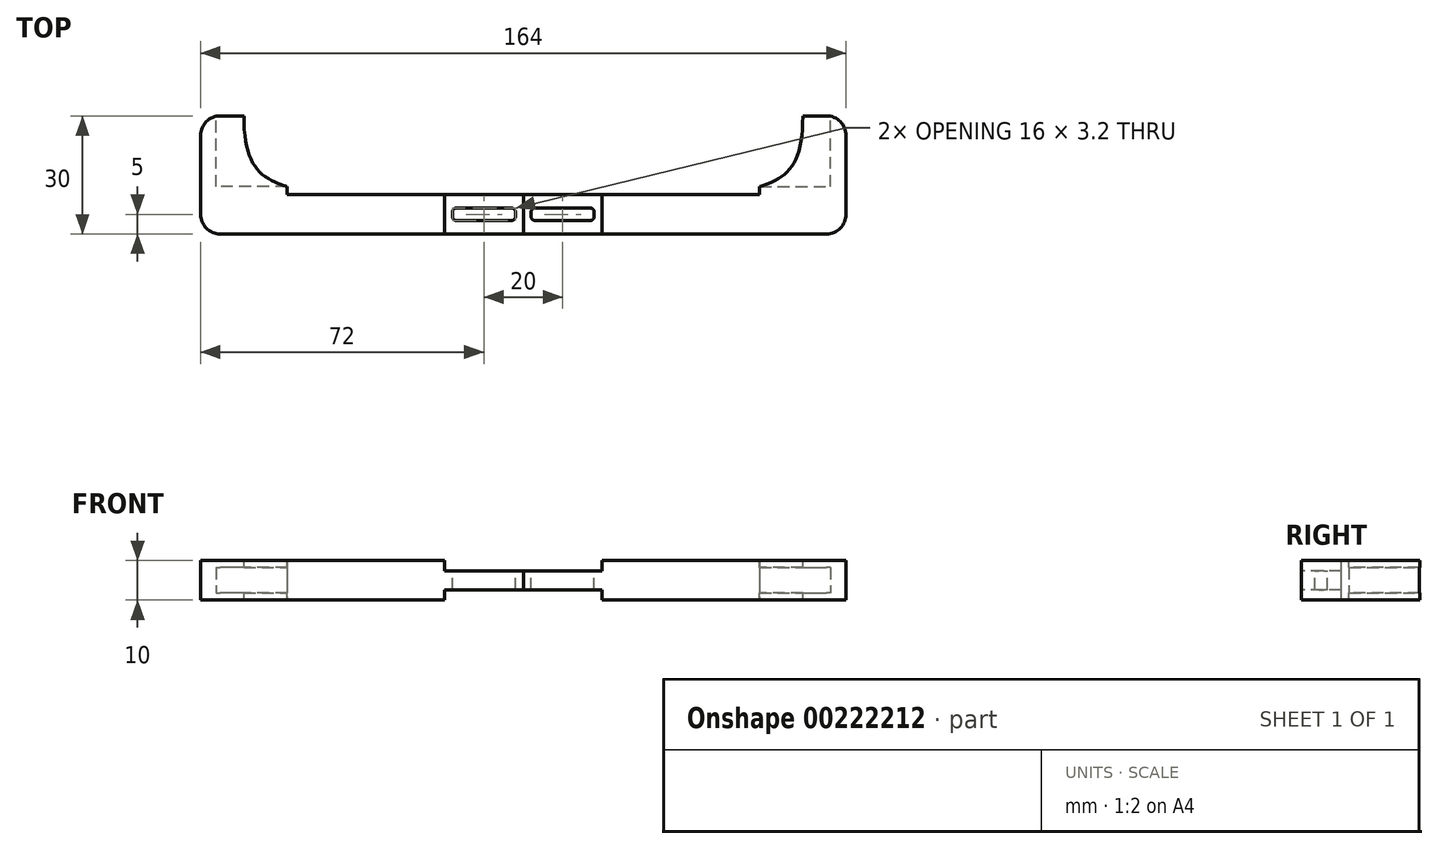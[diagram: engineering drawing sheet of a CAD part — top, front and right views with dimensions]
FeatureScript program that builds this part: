
annotation { "Feature Type Name" : "Feature", "Feature Type Description" : "" }
export const myFeature = defineFeature(function(context is Context, id is Id, definition is map)
    precondition{}
    {
        {
            var Q0;
            Q0=qCreatedBy(makeId("Top.planeOp"),FACE);
            var sketch = newSketch(context, id + "F0", { "sketchPlane" : qUnion([Q0])});
            skLineSegment(sketch, "E0.bottom", {"start": v(-11, 15) * mm, "end": v(11, 15) * mm});
            skLineSegment(sketch, "E0.top", {"start": v(-11, -15) * mm, "end": v(11, -15) * mm});
            skLineSegment(sketch, "E0.left", {"start": v(-11, 15) * mm, "end": v(-11, -15) * mm});
            skLineSegment(sketch, "E0.right", {"start": v(11, 15) * mm, "end": v(11, -15) * mm});
            skPoint(sketch, "E1", {"position": v(0, 15) * mm});
            skPoint(sketch, "E2", {"position": v(-11, 0) * mm});
            skSolve(sketch);
        }
        {
            var Q0;
            Q0=makeQuery(id+"F0.imprint","IMPRINT",FACE,{"disambiguationData":[TD([[makeQuery(id+"F0.imprint","IMPRINT",EDGE,{"derivedFrom":sQuery(id+"F0.wireOp",EDGE,"E0.bottom")}),-1.0]])]});
            extrude(context, id + "F1", {"entities" : qUnion([Q0]), "endBound" : BoundingType.SYMMETRIC, "depth" : 10 * mm});
        }
        {
            var Q0;
            Q0=makeQuery(id+"F1.opExtrude","SWEPT_FACE",FACE,{"disambiguationData":[OSD([sQuery(id+"F0.wireOp",EDGE,"E0.bottom")])]});
            var sketch = newSketch(context, id + "F2", { "sketchPlane" : qUnion([Q0])});
            skLineSegment(sketch, "E3.bottom", {"start": v(11, 3.25) * mm, "end": v(-7, 3.25) * mm});
            skLineSegment(sketch, "E3.top", {"start": v(11, -3.25) * mm, "end": v(-7, -3.25) * mm});
            skLineSegment(sketch, "E3.left", {"start": v(11, 3.25) * mm, "end": v(11, -3.25) * mm});
            skLineSegment(sketch, "E3.right", {"start": v(-7, 3.25) * mm, "end": v(-7, -3.25) * mm});
            skPoint(sketch, "E4", {"position": v(11, 0) * mm});
            skSolve(sketch);
        }
        {
            var Q0;
            Q0=makeQuery(id+"F2.imprint","IMPRINT",FACE,{"disambiguationData":[TD([[makeQuery(id+"F2.imprint","IMPRINT",EDGE,{"derivedFrom":sQuery(id+"F2.wireOp",EDGE,"E3.bottom")}),1.0]])]});
            extrude(context, id + "F3", {"entities" : qUnion([Q0]), "operationType" : NewBodyOperationType.REMOVE, "oppositeDirection" : true, "depth" : 18 * mm});
        }
        {
            var Q0;
            Q0=makeQuery(id+"F1.opExtrude","SWEPT_FACE",FACE,{"disambiguationData":[OSD([sQuery(id+"F0.wireOp",EDGE,"E0.left")])]});
            var sketch = newSketch(context, id + "F4", { "sketchPlane" : qUnion([Q0])});
            skLineSegment(sketch, "E5.bottom", {"start": v(15, 5) * mm, "end": v(5, 5) * mm});
            skLineSegment(sketch, "E5.top", {"start": v(15, -5) * mm, "end": v(5, -5) * mm});
            skLineSegment(sketch, "E5.left", {"start": v(15, 5) * mm, "end": v(15, -5) * mm});
            skLineSegment(sketch, "E5.right", {"start": v(5, 5) * mm, "end": v(5, -5) * mm});
            skSolve(sketch);
        }
        {
            var Q0;
            Q0=makeQuery(id+"F4.imprint","IMPRINT",FACE,{"disambiguationData":[TD([[makeQuery(id+"F4.imprint","IMPRINT",EDGE,{"derivedFrom":sQuery(id+"F4.wireOp",EDGE,"E5.bottom")}),-1.0]])]});
            extrude(context, id + "F5", {"entities" : qUnion([Q0]), "operationType" : NewBodyOperationType.ADD, "depth" : 40 * mm});
        }
        {
            var Q0;
            Q0=makeQuery(id+"F5.opExtrude","CAP_FACE",FACE,{"disambiguationData":[OSD([sQuery(id+"F4.wireOp",EDGE,"E5.bottom"),sQuery(id+"F4.wireOp",EDGE,"E5.top"),sQuery(id+"F4.wireOp",EDGE,"E5.left"),sQuery(id+"F4.wireOp",EDGE,"E5.right")])],"isStart":false});
            var sketch = newSketch(context, id + "F6", { "sketchPlane" : qUnion([Q0])});
            skLineSegment(sketch, "E6.bottom", {"start": v(5, 2.4) * mm, "end": v(15, 2.4) * mm});
            skLineSegment(sketch, "E6.top", {"start": v(5, -2.4) * mm, "end": v(15, -2.4) * mm});
            skLineSegment(sketch, "E6.left", {"start": v(5, 2.4) * mm, "end": v(5, -2.4) * mm});
            skLineSegment(sketch, "E6.right", {"start": v(15, 2.4) * mm, "end": v(15, -2.4) * mm});
            skPoint(sketch, "E7", {"position": v(5, 0) * mm});
            skSolve(sketch);
        }
        {
            var Q0;
            Q0=makeQuery(id+"F6.imprint","IMPRINT",FACE,{"disambiguationData":[TD([[makeQuery(id+"F6.imprint","IMPRINT",EDGE,{"derivedFrom":sQuery(id+"F6.wireOp",EDGE,"E6.bottom")}),-1.0]])]});
            extrude(context, id + "F7", {"entities" : qUnion([Q0]), "operationType" : NewBodyOperationType.ADD, "depth" : 20 * mm});
        }
        {
            var Q0;
            Q0=makeQuery(id+"F7.opExtrude","SWEPT_FACE",FACE,{"disambiguationData":[OSD([sQuery(id+"F6.wireOp",EDGE,"E6.bottom")])]});
            var sketch = newSketch(context, id + "F8", { "sketchPlane" : qUnion([Q0])});
            skLineSegment(sketch, "E8.bottom", {"start": v(-68, -8.4) * mm, "end": v(-54, -8.4) * mm});
            skLineSegment(sketch, "E8.top", {"start": v(-68, -11.6) * mm, "end": v(-54, -11.6) * mm});
            skLineSegment(sketch, "E8.left", {"start": v(-69, -9.4) * mm, "end": v(-69, -10.6) * mm});
            skLineSegment(sketch, "E8.right", {"start": v(-53, -9.4) * mm, "end": v(-53, -10.6) * mm});
            skPoint(sketch, "E9", {"position": v(-61, -8.4) * mm});
            skPoint(sketch, "E10", {"position": v(-61, -5) * mm});
            skPoint(sketch, "E11", {"position": v(-69, -10) * mm});
            skPoint(sketch, "E12", {"position": v(-71, -10) * mm});
            skPoint(sketch, "E13.visualSharp", {"position": v(-53, -8.4) * mm});
            skArc(sketch, "E13.filletArc", {"start": v(-53, -9.4) * mm, "mid": v(-53.3, -8.7) * mm, "end": v(-54, -8.4) * mm});
            skPoint(sketch, "E14.visualSharp", {"position": v(-53, -11.6) * mm});
            skArc(sketch, "E14.filletArc", {"start": v(-54, -11.6) * mm, "mid": v(-53.3, -11.3) * mm, "end": v(-53, -10.6) * mm});
            skPoint(sketch, "E15.visualSharp", {"position": v(-69, -11.6) * mm});
            skArc(sketch, "E15.filletArc", {"start": v(-69, -10.6) * mm, "mid": v(-68.7, -11.3) * mm, "end": v(-68, -11.6) * mm});
            skPoint(sketch, "E16.visualSharp", {"position": v(-69, -8.4) * mm});
            skArc(sketch, "E16.filletArc", {"start": v(-68, -8.4) * mm, "mid": v(-68.7, -8.7) * mm, "end": v(-69, -9.4) * mm});
            skSolve(sketch);
        }
        {
            var Q0;
            Q0=makeQuery(id+"F8.imprint","IMPRINT",FACE,{"disambiguationData":[TD([[makeQuery(id+"F8.imprint","IMPRINT",EDGE,{"derivedFrom":sQuery(id+"F8.wireOp",EDGE,"E8.bottom")}),-1.0]])]});
            extrude(context, id + "F9", {"entities" : qUnion([Q0]), "operationType" : NewBodyOperationType.REMOVE, "endBound" : BoundingType.UP_TO_NEXT, "oppositeDirection" : true, "depth" : 25 * mm});
        }
        {
            var Q0;
            Q0=makeQuery(id+"F5.boolean.opBoolean","MERGE",FACE,{"derivedFrom":[makeQuery(id+"F1.opExtrude","CAP_FACE",FACE,{"disambiguationData":[OSD([sQuery(id+"F0.wireOp",EDGE,"E0.bottom"),sQuery(id+"F0.wireOp",EDGE,"E0.top"),sQuery(id+"F0.wireOp",EDGE,"E0.left"),sQuery(id+"F0.wireOp",EDGE,"E0.right")])],"isStart":false}),makeQuery(id+"F5.opExtrude","SWEPT_FACE",FACE,{"disambiguationData":[OSD([sQuery(id+"F4.wireOp",EDGE,"E5.bottom")])]})]});
            var sketch = newSketch(context, id + "F10", { "sketchPlane" : qUnion([Q0])});
            skFitSpline(sketch, "E17", {"points": [v(0, 15) * mm, v(-5.9, -0.75) * mm, v(-11, -3) * mm], "startDerivative": vector(0, -42.33) * mm, "endDerivative": vector(-0.04, -0.45) * mm});
            skSolve(sketch);
        }
        {
            var Q0;
            {var subQ0=sQuery(id+"F10.wireOp",EDGE,"E17");Q0=makeQuery(id+"F10.imprint","IMPRINT",FACE,{"disambiguationData":[TD([[makeQuery(id+"F10.imprint","IMPRINT",EDGE,{"derivedFrom":subQ0}),-1.0]])]});}
            var Q1;
            Q1=makeQuery(id+"F5.boolean.opBoolean","MERGE",FACE,{"derivedFrom":[makeQuery(id+"F1.opExtrude","CAP_FACE",FACE,{"disambiguationData":[OSD([sQuery(id+"F0.wireOp",EDGE,"E0.bottom"),sQuery(id+"F0.wireOp",EDGE,"E0.top"),sQuery(id+"F0.wireOp",EDGE,"E0.left"),sQuery(id+"F0.wireOp",EDGE,"E0.right")])],"isStart":true}),makeQuery(id+"F5.opExtrude","SWEPT_FACE",FACE,{"disambiguationData":[OSD([sQuery(id+"F4.wireOp",EDGE,"E5.top")])]})]});
            extrude(context, id + "F11", {"entities" : qUnion([Q0]), "operationType" : NewBodyOperationType.REMOVE, "endBound" : BoundingType.UP_TO_SURFACE, "oppositeDirection" : true, "endBoundEntityFace" : qUnion([Q1]), "depth" : 25 * mm});
        }
        {
            var Q0;
            Q0=makeQuery(id+"F1.opExtrude","SWEPT_EDGE",EDGE,{"disambiguationData":[OSD([sQuery(id+"F0.wireOp",EDGE,"E0.top"),sQuery(id+"F0.wireOp",EDGE,"E0.right")])]});
            fillet(context, id + "F12", {"entities" : qUnion([Q0]), "radius" : 5 * mm, "tangentPropagation" : true, "allowEdgeOverflow" : false});
        }
        {
            var Q0;
            Q0=makeQuery(id+"F1.opExtrude","SWEPT_EDGE",EDGE,{"disambiguationData":[OSD([sQuery(id+"F0.wireOp",EDGE,"E0.bottom"),sQuery(id+"F0.wireOp",EDGE,"E0.right")])]});
            fillet(context, id + "F13", {"entities" : qUnion([Q0]), "radius" : 5 * mm, "tangentPropagation" : true, "allowEdgeOverflow" : false});
        }
        {
            var Q0;
            Q0=makeQuery(id+"F1.opExtrude","SWEPT_BODY",BODY,{"disambiguationData":[OSD([sQuery(id+"F0.wireOp",EDGE,"E0.bottom"),sQuery(id+"F0.wireOp",EDGE,"E0.top"),sQuery(id+"F0.wireOp",EDGE,"E0.left"),sQuery(id+"F0.wireOp",EDGE,"E0.right")])]});
            var Q1;
            Q1=makeQuery(id+"F7.opExtrude","CAP_FACE",FACE,{"disambiguationData":[OSD([sQuery(id+"F6.wireOp",EDGE,"E6.bottom"),sQuery(id+"F6.wireOp",EDGE,"E6.top"),sQuery(id+"F6.wireOp",EDGE,"E6.left"),sQuery(id+"F6.wireOp",EDGE,"E6.right")])],"isStart":false});
            mirror(context, id + "F14", {"entities" : qUnion([Q0]), "mirrorPlane" : qUnion([Q1])});
        }
    });
